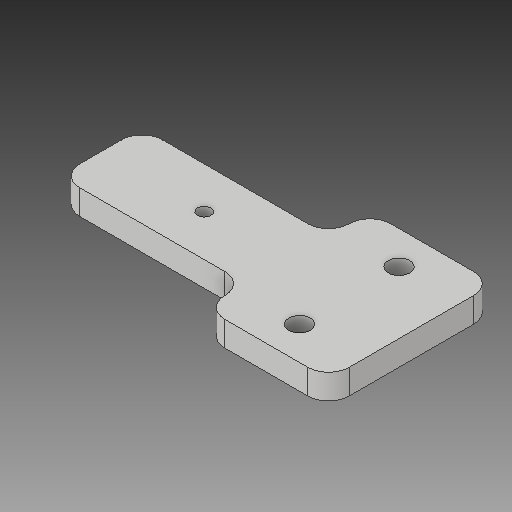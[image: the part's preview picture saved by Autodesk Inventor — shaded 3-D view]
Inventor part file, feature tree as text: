
AUTODESK INVENTOR PART (.ipt)
format: ipt  version: 2018 (Build 220112000, 112)  size: 119,296 bytes
history: native  units: mm
features: extrude x1, sketch x1
ambient origin geometry x8: Origin, YZ Plane, XZ Plane, XY Plane, X Axis, Y Axis, Z Axis, Center Point
bodies: Solid1 (feature_tree)
feature tree (2):
  extrude  "Extrusion1"  [1 undecoded]
  sketch  "Sketch1"  dims[d0=6.0mm d1=0.0mm]
note: 1 required parameter value undecoded (feature->parameter linkage not recoverable at this tier; creation-order binding heuristic only, values carry confidence <= 0.55)
